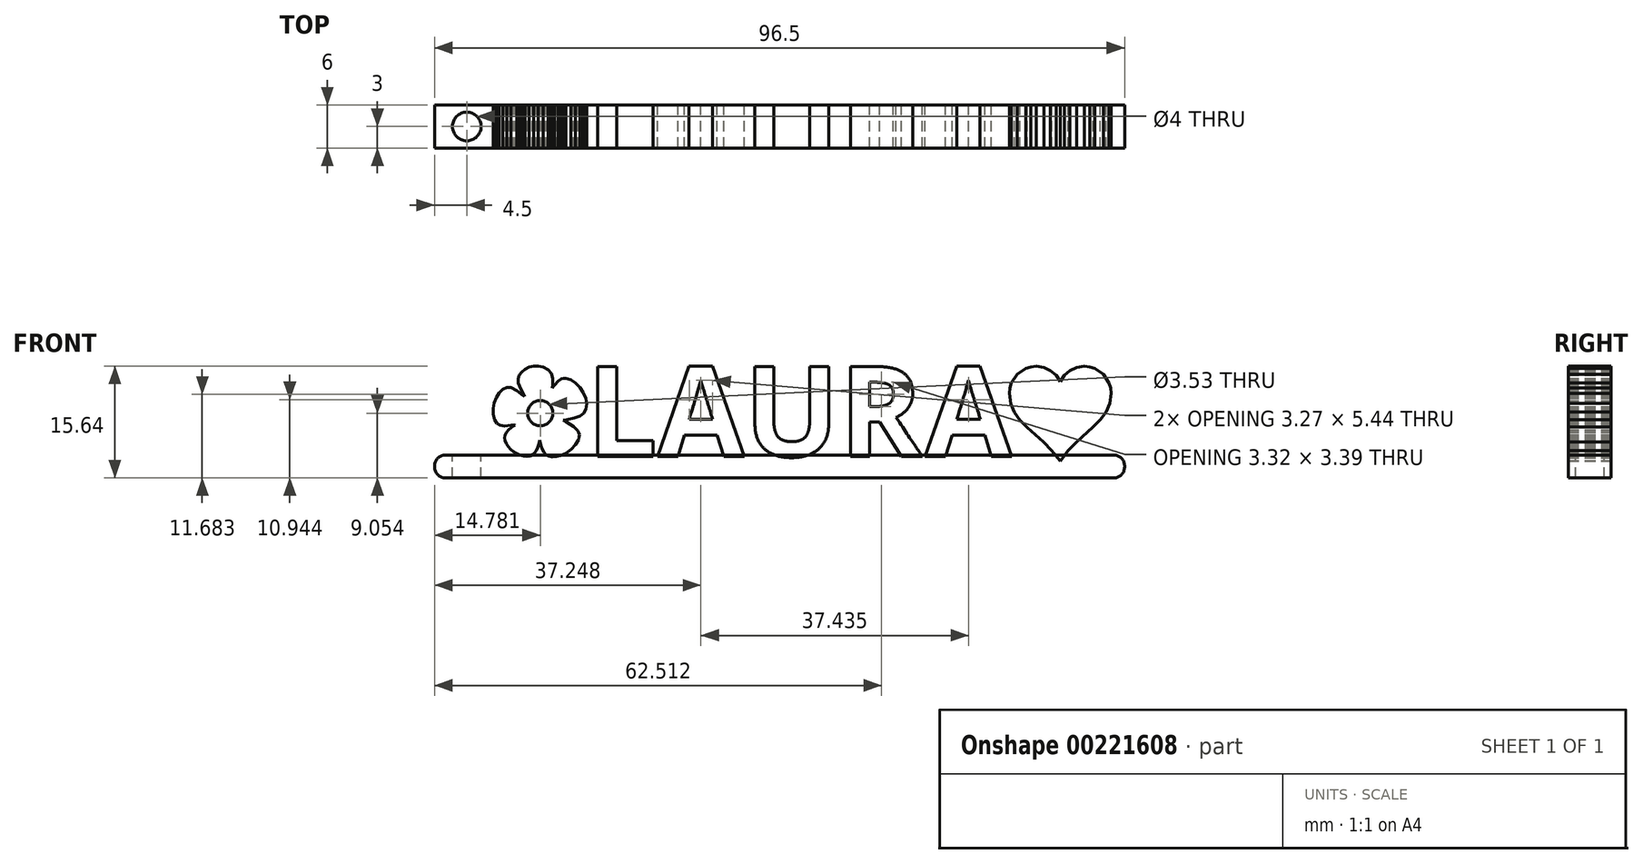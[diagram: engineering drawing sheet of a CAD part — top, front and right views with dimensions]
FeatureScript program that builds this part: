
annotation { "Feature Type Name" : "Feature", "Feature Type Description" : "" }
export const myFeature = defineFeature(function(context is Context, id is Id, definition is map)
    precondition{}
    {
        {
            var Q0;
            Q0=qCreatedBy(makeId("Front.planeOp"),FACE);
            var sketch = newSketch(context, id + "F0", { "sketchPlane" : qUnion([Q0])});
            skText(sketch, "E0", { "text": "   LAURA", "fontName": "OpenSans-Bold.ttf"});
            skLineSegment(sketch, "E1.0.0", {"start": v(-9.3, 0.1) * mm, "end": v(-8.53, 0.46) * mm});
            skLineSegment(sketch, "E1.0.1", {"start": v(-8.53, 0.46) * mm, "end": v(-7.79, 1.02) * mm});
            skLineSegment(sketch, "E1.0.2", {"start": v(-7.79, 1.02) * mm, "end": v(-7.18, 1.67) * mm});
            skLineSegment(sketch, "E1.0.3", {"start": v(-7.18, 1.67) * mm, "end": v(-6.78, 2.35) * mm});
            skLineSegment(sketch, "E1.0.4", {"start": v(-6.78, 2.35) * mm, "end": v(-6.68, 2.7) * mm});
            skLineSegment(sketch, "E1.0.5", {"start": v(-6.68, 2.7) * mm, "end": v(-6.67, 3.02) * mm});
            skLineSegment(sketch, "E1.0.6", {"start": v(-6.67, 3.02) * mm, "end": v(-6.73, 3.33) * mm});
            skLineSegment(sketch, "E1.0.7", {"start": v(-6.73, 3.33) * mm, "end": v(-6.89, 3.62) * mm});
            skLineSegment(sketch, "E1.0.8", {"start": v(-6.89, 3.62) * mm, "end": v(-7.48, 4.2) * mm});
            skLineSegment(sketch, "E1.0.9", {"start": v(-7.48, 4.2) * mm, "end": v(-8.5, 4.79) * mm});
            skLineSegment(sketch, "E1.0.10", {"start": v(-8.5, 4.79) * mm, "end": v(-8.93, 5.06) * mm});
            skLineSegment(sketch, "E1.0.11", {"start": v(-8.93, 5.06) * mm, "end": v(-8.42, 5.16) * mm});
            skLineSegment(sketch, "E1.0.12", {"start": v(-8.42, 5.16) * mm, "end": v(-7.31, 5.37) * mm});
            skLineSegment(sketch, "E1.0.13", {"start": v(-7.31, 5.37) * mm, "end": v(-6.55, 5.65) * mm});
            skLineSegment(sketch, "E1.0.14", {"start": v(-6.55, 5.65) * mm, "end": v(-6.05, 6.04) * mm});
            skLineSegment(sketch, "E1.0.15", {"start": v(-6.05, 6.04) * mm, "end": v(-5.76, 6.58) * mm});
            skLineSegment(sketch, "E1.0.16", {"start": v(-5.76, 6.58) * mm, "end": v(-5.64, 7.33) * mm});
            skLineSegment(sketch, "E1.0.17", {"start": v(-5.64, 7.33) * mm, "end": v(-5.78, 8.14) * mm});
            skLineSegment(sketch, "E1.0.18", {"start": v(-5.78, 8.14) * mm, "end": v(-6.1, 8.93) * mm});
            skLineSegment(sketch, "E1.0.19", {"start": v(-6.1, 8.93) * mm, "end": v(-6.6, 9.67) * mm});
            skLineSegment(sketch, "E1.0.20", {"start": v(-6.6, 9.67) * mm, "end": v(-7.2, 10.28) * mm});
            skLineSegment(sketch, "E1.0.21", {"start": v(-7.2, 10.28) * mm, "end": v(-7.86, 10.72) * mm});
            skLineSegment(sketch, "E1.0.22", {"start": v(-7.86, 10.72) * mm, "end": v(-8.55, 10.93) * mm});
            skLineSegment(sketch, "E1.0.23", {"start": v(-8.55, 10.93) * mm, "end": v(-8.88, 10.93) * mm});
            skLineSegment(sketch, "E1.0.24", {"start": v(-8.88, 10.93) * mm, "end": v(-9.2, 10.85) * mm});
            skLineSegment(sketch, "E1.0.25", {"start": v(-9.2, 10.85) * mm, "end": v(-9.65, 10.56) * mm});
            skLineSegment(sketch, "E1.0.26", {"start": v(-9.65, 10.56) * mm, "end": v(-10.14, 9.98) * mm});
            skLineSegment(sketch, "E1.0.27", {"start": v(-10.14, 9.98) * mm, "end": v(-10.45, 9.58) * mm});
            skLineSegment(sketch, "E1.0.28", {"start": v(-10.45, 9.58) * mm, "end": v(-10.4, 10.03) * mm});
            skLineSegment(sketch, "E1.0.29", {"start": v(-10.4, 10.03) * mm, "end": v(-10.4, 10.93) * mm});
            skLineSegment(sketch, "E1.0.30", {"start": v(-10.4, 10.93) * mm, "end": v(-10.6, 11.63) * mm});
            skLineSegment(sketch, "E1.0.31", {"start": v(-10.6, 11.63) * mm, "end": v(-11.04, 12.15) * mm});
            skLineSegment(sketch, "E1.0.32", {"start": v(-11.04, 12.15) * mm, "end": v(-11.71, 12.5) * mm});
            skLineSegment(sketch, "E1.0.33", {"start": v(-11.71, 12.5) * mm, "end": v(-12.4, 12.64) * mm});
            skLineSegment(sketch, "E1.0.34", {"start": v(-12.4, 12.64) * mm, "end": v(-13.07, 12.62) * mm});
            skLineSegment(sketch, "E1.0.35", {"start": v(-13.07, 12.62) * mm, "end": v(-13.7, 12.47) * mm});
            skLineSegment(sketch, "E1.0.36", {"start": v(-13.7, 12.47) * mm, "end": v(-14.26, 12.2) * mm});
            skLineSegment(sketch, "E1.0.37", {"start": v(-14.26, 12.2) * mm, "end": v(-14.72, 11.83) * mm});
            skLineSegment(sketch, "E1.0.38", {"start": v(-14.72, 11.83) * mm, "end": v(-15.05, 11.38) * mm});
            skLineSegment(sketch, "E1.0.39", {"start": v(-15.05, 11.38) * mm, "end": v(-15.22, 10.87) * mm});
            skLineSegment(sketch, "E1.0.40", {"start": v(-15.22, 10.87) * mm, "end": v(-15.2, 10.3) * mm});
            skLineSegment(sketch, "E1.0.41", {"start": v(-15.2, 10.3) * mm, "end": v(-14.83, 9.4) * mm});
            skLineSegment(sketch, "E1.0.42", {"start": v(-14.83, 9.4) * mm, "end": v(-14.35, 8.55) * mm});
            skLineSegment(sketch, "E1.0.43", {"start": v(-14.35, 8.55) * mm, "end": v(-14.3, 8.4) * mm});
            skLineSegment(sketch, "E1.0.44", {"start": v(-14.3, 8.4) * mm, "end": v(-14.48, 8.53) * mm});
            skLineSegment(sketch, "E1.0.45", {"start": v(-14.48, 8.53) * mm, "end": v(-15.4, 9.23) * mm});
            skLineSegment(sketch, "E1.0.46", {"start": v(-15.4, 9.23) * mm, "end": v(-16.22, 9.63) * mm});
            skLineSegment(sketch, "E1.0.47", {"start": v(-16.22, 9.63) * mm, "end": v(-16.8, 9.63) * mm});
            skLineSegment(sketch, "E1.0.48", {"start": v(-16.8, 9.63) * mm, "end": v(-17.36, 9.37) * mm});
            skLineSegment(sketch, "E1.0.49", {"start": v(-17.36, 9.37) * mm, "end": v(-17.85, 8.9) * mm});
            skLineSegment(sketch, "E1.0.50", {"start": v(-17.85, 8.9) * mm, "end": v(-18.26, 8.26) * mm});
            skLineSegment(sketch, "E1.0.51", {"start": v(-18.26, 8.26) * mm, "end": v(-18.56, 7.51) * mm});
            skLineSegment(sketch, "E1.0.52", {"start": v(-18.56, 7.51) * mm, "end": v(-18.72, 6.71) * mm});
            skLineSegment(sketch, "E1.0.53", {"start": v(-18.72, 6.71) * mm, "end": v(-18.72, 5.9) * mm});
            skLineSegment(sketch, "E1.0.54", {"start": v(-18.72, 5.9) * mm, "end": v(-18.52, 5.16) * mm});
            skLineSegment(sketch, "E1.0.55", {"start": v(-18.52, 5.16) * mm, "end": v(-18.2, 4.64) * mm});
            skLineSegment(sketch, "E1.0.56", {"start": v(-18.2, 4.64) * mm, "end": v(-17.75, 4.36) * mm});
            skLineSegment(sketch, "E1.0.57", {"start": v(-17.75, 4.36) * mm, "end": v(-17.1, 4.27) * mm});
            skLineSegment(sketch, "E1.0.58", {"start": v(-17.1, 4.27) * mm, "end": v(-16.21, 4.37) * mm});
            skLineSegment(sketch, "E1.0.59", {"start": v(-16.21, 4.37) * mm, "end": v(-15.7, 4.43) * mm});
            skLineSegment(sketch, "E1.0.60", {"start": v(-15.7, 4.43) * mm, "end": v(-15.67, 4.4) * mm});
            skLineSegment(sketch, "E1.0.61", {"start": v(-15.67, 4.4) * mm, "end": v(-15.78, 4.33) * mm});
            skLineSegment(sketch, "E1.0.62", {"start": v(-15.78, 4.33) * mm, "end": v(-16.17, 4.07) * mm});
            skLineSegment(sketch, "E1.0.63", {"start": v(-16.17, 4.07) * mm, "end": v(-16.55, 3.71) * mm});
            skLineSegment(sketch, "E1.0.64", {"start": v(-16.55, 3.71) * mm, "end": v(-16.87, 3.33) * mm});
            skLineSegment(sketch, "E1.0.65", {"start": v(-16.87, 3.33) * mm, "end": v(-17.04, 3) * mm});
            skLineSegment(sketch, "E1.0.66", {"start": v(-17.04, 3) * mm, "end": v(-17.08, 2.6) * mm});
            skLineSegment(sketch, "E1.0.67", {"start": v(-17.08, 2.6) * mm, "end": v(-17.02, 2.2) * mm});
            skLineSegment(sketch, "E1.0.68", {"start": v(-17.02, 2.2) * mm, "end": v(-16.87, 1.78) * mm});
            skLineSegment(sketch, "E1.0.69", {"start": v(-16.87, 1.78) * mm, "end": v(-16.62, 1.39) * mm});
            skLineSegment(sketch, "E1.0.70", {"start": v(-16.62, 1.39) * mm, "end": v(-16.3, 1.02) * mm});
            skLineSegment(sketch, "E1.0.71", {"start": v(-16.3, 1.02) * mm, "end": v(-15.9, 0.69) * mm});
            skLineSegment(sketch, "E1.0.72", {"start": v(-15.9, 0.69) * mm, "end": v(-15.45, 0.4) * mm});
            skLineSegment(sketch, "E1.0.73", {"start": v(-15.45, 0.4) * mm, "end": v(-14.95, 0.2) * mm});
            skLineSegment(sketch, "E1.0.74", {"start": v(-14.95, 0.2) * mm, "end": v(-14.44, 0.06) * mm});
            skLineSegment(sketch, "E1.0.75", {"start": v(-14.44, 0.06) * mm, "end": v(-13.98, 0.02) * mm});
            skLineSegment(sketch, "E1.0.76", {"start": v(-13.98, 0.02) * mm, "end": v(-13.58, 0.08) * mm});
            skLineSegment(sketch, "E1.0.77", {"start": v(-13.58, 0.08) * mm, "end": v(-13.23, 0.23) * mm});
            skLineSegment(sketch, "E1.0.78", {"start": v(-13.23, 0.23) * mm, "end": v(-12.92, 0.49) * mm});
            skLineSegment(sketch, "E1.0.79", {"start": v(-12.92, 0.49) * mm, "end": v(-12.67, 0.84) * mm});
            skLineSegment(sketch, "E1.0.80", {"start": v(-12.67, 0.84) * mm, "end": v(-12.46, 1.28) * mm});
            skLineSegment(sketch, "E1.0.81", {"start": v(-12.46, 1.28) * mm, "end": v(-12.3, 1.83) * mm});
            skLineSegment(sketch, "E1.0.82", {"start": v(-12.3, 1.83) * mm, "end": v(-12.19, 2.26) * mm});
            skLineSegment(sketch, "E1.0.83", {"start": v(-12.19, 2.26) * mm, "end": v(-12.13, 2.1) * mm});
            skLineSegment(sketch, "E1.0.84", {"start": v(-12.13, 2.1) * mm, "end": v(-12.01, 1.53) * mm});
            skLineSegment(sketch, "E1.0.85", {"start": v(-12.01, 1.53) * mm, "end": v(-11.82, 1) * mm});
            skLineSegment(sketch, "E1.0.86", {"start": v(-11.82, 1) * mm, "end": v(-11.6, 0.55) * mm});
            skLineSegment(sketch, "E1.0.87", {"start": v(-11.6, 0.55) * mm, "end": v(-11.35, 0.26) * mm});
            skLineSegment(sketch, "E1.0.88", {"start": v(-11.35, 0.26) * mm, "end": v(-10.95, 0.05) * mm});
            skLineSegment(sketch, "E1.0.89", {"start": v(-10.95, 0.05) * mm, "end": v(-10.46, -0.04) * mm});
            skLineSegment(sketch, "E1.0.90", {"start": v(-10.46, -0.04) * mm, "end": v(-9.9, -0.03) * mm});
            skLineSegment(sketch, "E1.0.91", {"start": v(-9.9, -0.03) * mm, "end": v(-9.3, 0.1) * mm});
            skCircle(sketch, "E2", {"center": v(-12.12, 6.05) * mm, "radius": 1.77 * mm});
            skLineSegment(sketch, "E3", {"start": v(57.24, 12.6) * mm, "end": v(56.48, 12.52) * mm});
            skLineSegment(sketch, "E4", {"start": v(56.48, 12.52) * mm, "end": v(55.78, 12.3) * mm});
            skLineSegment(sketch, "E5", {"start": v(55.78, 12.3) * mm, "end": v(54.58, 11.5) * mm});
            skLineSegment(sketch, "E6", {"start": v(54.58, 11.5) * mm, "end": v(53.77, 10.3) * mm});
            skLineSegment(sketch, "E7", {"start": v(53.77, 10.3) * mm, "end": v(53.55, 9.59) * mm});
            skLineSegment(sketch, "E8", {"start": v(53.55, 9.59) * mm, "end": v(53.48, 8.83) * mm});
            skLineSegment(sketch, "E9", {"start": v(53.48, 8.83) * mm, "end": v(53.66, 7.39) * mm});
            skLineSegment(sketch, "E10", {"start": v(53.66, 7.39) * mm, "end": v(54.19, 6.16) * mm});
            skLineSegment(sketch, "E11", {"start": v(54.19, 6.16) * mm, "end": v(54.97, 5.08) * mm});
            skLineSegment(sketch, "E12", {"start": v(54.97, 5.08) * mm, "end": v(55.95, 4.08) * mm});
            skLineSegment(sketch, "E13", {"start": v(55.95, 4.08) * mm, "end": v(58.25, 2.03) * mm});
            skLineSegment(sketch, "E14", {"start": v(58.25, 2.03) * mm, "end": v(59.44, 0.82) * mm});
            skLineSegment(sketch, "E15", {"start": v(59.44, 0.82) * mm, "end": v(60.56, -0.59) * mm});
            skLineSegment(sketch, "E16", {"start": v(60.56, -0.59) * mm, "end": v(60.6, -0.65) * mm});
            skLineSegment(sketch, "E17", {"start": v(60.6, -0.65) * mm, "end": v(60.65, -0.59) * mm});
            skLineSegment(sketch, "E18", {"start": v(60.65, -0.59) * mm, "end": v(61.72, 0.82) * mm});
            skLineSegment(sketch, "E19", {"start": v(61.72, 0.82) * mm, "end": v(62.89, 2.03) * mm});
            skLineSegment(sketch, "E20", {"start": v(62.89, 2.03) * mm, "end": v(65.2, 4.12) * mm});
            skLineSegment(sketch, "E21", {"start": v(65.2, 4.12) * mm, "end": v(66.2, 5.13) * mm});
            skLineSegment(sketch, "E22", {"start": v(66.2, 5.13) * mm, "end": v(67, 6.21) * mm});
            skLineSegment(sketch, "E23", {"start": v(67, 6.21) * mm, "end": v(67.53, 7.42) * mm});
            skLineSegment(sketch, "E24", {"start": v(67.53, 7.42) * mm, "end": v(67.73, 8.83) * mm});
            skLineSegment(sketch, "E25", {"start": v(67.73, 8.83) * mm, "end": v(67.65, 9.59) * mm});
            skLineSegment(sketch, "E26", {"start": v(67.65, 9.59) * mm, "end": v(67.43, 10.3) * mm});
            skLineSegment(sketch, "E27", {"start": v(67.43, 10.3) * mm, "end": v(66.62, 11.5) * mm});
            skLineSegment(sketch, "E28", {"start": v(66.62, 11.5) * mm, "end": v(65.43, 12.3) * mm});
            skLineSegment(sketch, "E29", {"start": v(65.43, 12.3) * mm, "end": v(64.72, 12.52) * mm});
            skLineSegment(sketch, "E30", {"start": v(64.72, 12.52) * mm, "end": v(63.96, 12.6) * mm});
            skLineSegment(sketch, "E31", {"start": v(63.96, 12.6) * mm, "end": v(62.9, 12.44) * mm});
            skLineSegment(sketch, "E32", {"start": v(62.9, 12.44) * mm, "end": v(61.96, 12.01) * mm});
            skLineSegment(sketch, "E33", {"start": v(61.96, 12.01) * mm, "end": v(61.18, 11.35) * mm});
            skLineSegment(sketch, "E34", {"start": v(61.18, 11.35) * mm, "end": v(60.6, 10.5) * mm});
            skLineSegment(sketch, "E35", {"start": v(60.6, 10.5) * mm, "end": v(60.02, 11.35) * mm});
            skLineSegment(sketch, "E36", {"start": v(60.02, 11.35) * mm, "end": v(59.24, 12.01) * mm});
            skLineSegment(sketch, "E37", {"start": v(59.24, 12.01) * mm, "end": v(58.3, 12.44) * mm});
            skLineSegment(sketch, "E38", {"start": v(58.3, 12.44) * mm, "end": v(57.24, 12.6) * mm});
            skLineSegment(sketch, "E39", {"start": v(54.6, 12.67) * mm, "end": v(72.98, 12.67) * mm, "construction": true});
            const initialGuessF0  = {"E0": [-0.0194, 0, 1, 0, 0.01267]};
            skSetInitialGuess(sketch, initialGuessF0);
            skSolve(sketch);
        }
        {
            var Q0;
            Q0=qSketchRegion(id+"F0",true);
            extrude(context, id + "F1", {"entities" : qUnion([Q0]), "endBound" : BoundingType.SYMMETRIC, "depth" : 6 * mm});
        }
        {
            var Q0;
            Q0=qCreatedBy(makeId("Top.planeOp"),FACE);
            var sketch = newSketch(context, id + "F2", { "sketchPlane" : qUnion([Q0])});
            skLineSegment(sketch, "E40.bottom", {"start": v(-19.4, 3) * mm, "end": v(69.6, 3) * mm});
            skLineSegment(sketch, "E40.top", {"start": v(-19.4, -3) * mm, "end": v(69.6, -3) * mm});
            skLineSegment(sketch, "E40.left", {"start": v(-19.4, 3) * mm, "end": v(-19.4, -3) * mm});
            skLineSegment(sketch, "E40.right", {"start": v(69.6, 3) * mm, "end": v(69.6, -3) * mm});
            skSolve(sketch);
        }
        {
            var Q0;
            Q0=makeQuery(id+"F2.imprint","IMPRINT",FACE,{"disambiguationData":[TD([[makeQuery(id+"F2.imprint","IMPRINT",EDGE,{"derivedFrom":sQuery(id+"F2.wireOp",EDGE,"E40.bottom")}),-1.0]])]});
            extrude(context, id + "F3", {"entities" : qUnion([Q0]), "depth" : 0.2 * mm});
        }
        {
            var Q0;
            Q0=makeQuery(id+"F3.opExtrude","CAP_FACE",FACE,{"disambiguationData":[OSD([sQuery(id+"F2.wireOp",EDGE,"E40.bottom"),sQuery(id+"F2.wireOp",EDGE,"E40.top"),sQuery(id+"F2.wireOp",EDGE,"E40.left"),sQuery(id+"F2.wireOp",EDGE,"E40.right")])],"isStart":true});
            extrude(context, id + "F4", {"entities" : qUnion([Q0]), "depth" : 3 * mm});
        }
        {
            var Q0;
            {var subQ0=sQuery(id+"F2.wireOp",EDGE,"E40.left");Q0=makeQuery(id+"FaVoHrOpcFZXiYX_6.opBoolean","MERGE",FACE,{"derivedFrom":[makeQuery(id+"F3.opExtrude","SWEPT_FACE",FACE,{"disambiguationData":[OSD([subQ0])]}),makeQuery(id+"F4.opExtrude","SWEPT_FACE",FACE,{"disambiguationData":[OSD([subQ0])]})]});}
            var sketch = newSketch(context, id + "F5", { "sketchPlane" : qUnion([Q0])});
            skLineSegment(sketch, "E41.bottom", {"start": v(-3, -3) * mm, "end": v(3, -3) * mm});
            skLineSegment(sketch, "E41.top", {"start": v(-3, 0.2) * mm, "end": v(3, 0.2) * mm});
            skLineSegment(sketch, "E41.left", {"start": v(-3, -3) * mm, "end": v(-3, 0.2) * mm});
            skLineSegment(sketch, "E41.right", {"start": v(3, -3) * mm, "end": v(3, 0.2) * mm});
            skSolve(sketch);
        }
        {
            var Q0;
            Q0=qSketchRegion(id+"F5",true);
            extrude(context, id + "F6", {"entities" : qUnion([Q0]), "operationType" : NewBodyOperationType.ADD, "depth" : 7.5 * mm});
        }
        {
            var Q0;
            Q0=makeQuery(id+"F6.opExtrude","CAP_EDGE",EDGE,{"disambiguationData":[OSD([sQuery(id+"F5.wireOp",EDGE,"E41.bottom")])],"isStart":false});
            var Q1;
            Q1=makeQuery(id+"F6.opExtrude","CAP_EDGE",EDGE,{"disambiguationData":[OSD([sQuery(id+"F5.wireOp",EDGE,"E41.top")])],"isStart":false});
            var Q2;
            Q2=makeQuery(id+"F4.opExtrude","CAP_EDGE",EDGE,{"disambiguationData":[OSD([sQuery(id+"F2.wireOp",EDGE,"E40.right")])],"isStart":false});
            fillet(context, id + "F7", {"entities" : qUnion([Q0, Q1, Q2]), "radius" : 1.5 * mm, "tangentPropagation" : true, "allowEdgeOverflow" : false});
        }
        {
            var Q0;
            {var subQ19=sQuery(id+"F2.wireOp",EDGE,"E40.top");var subQ20=sQuery(id+"F2.wireOp",EDGE,"E40.bottom");var subQ63=sQuery(id+"F0.wireOp",EDGE,"E0.sketch_text.stroke-2");var subQ66=sQuery(id+"F2.wireOp",EDGE,"E40.left");Q0=makeQuery(id+"F6.boolean.opBoolean","MERGE",FACE,{"derivedFrom":[makeQuery(id+"FaVoHrOpcFZXiYX_6.opBoolean","SPLIT",FACE,{"disambiguationData":[TD([makeQuery(id+"F1.opExtrude","SWEPT_FACE",FACE,{"disambiguationData":[OSD([subQ63])]})])],"derivedFrom":makeQuery(id+"F3.opExtrude","CAP_FACE",FACE,{"disambiguationData":[OSD([subQ20,subQ19,subQ66,sQuery(id+"F2.wireOp",EDGE,"E40.right")])],"isStart":false})}),makeQuery(id+"F6.opExtrude","SWEPT_FACE",FACE,{"disambiguationData":[OSD([sQuery(id+"F5.wireOp",EDGE,"E41.top")])]})]});}
            var sketch = newSketch(context, id + "F8", { "sketchPlane" : qUnion([Q0])});
            skCircle(sketch, "E42", {"center": v(-22.4, 0) * mm, "radius": 2 * mm});
            skSolve(sketch);
        }
        {
            var Q0;
            Q0=makeQuery(id+"F8.imprint","IMPRINT",FACE,{"disambiguationData":[TD([[makeQuery(id+"F8.imprint","IMPRINT",EDGE,{"derivedFrom":sQuery(id+"F8.wireOp",EDGE,"E42")}),1.0]])]});
            extrude(context, id + "F9", {"entities" : qUnion([Q0]), "operationType" : NewBodyOperationType.REMOVE, "oppositeDirection" : true, "depth" : 4 * mm});
        }
        {
            var Q0;
            Q0=makeQuery(id+"F3.opExtrude","CAP_EDGE",EDGE,{"disambiguationData":[OSD([sQuery(id+"F2.wireOp",EDGE,"E40.right")])],"isStart":false});
            fillet(context, id + "F10", {"entities" : qUnion([Q0]), "radius" : 1.5 * mm, "tangentPropagation" : true, "allowEdgeOverflow" : false});
        }
    });
